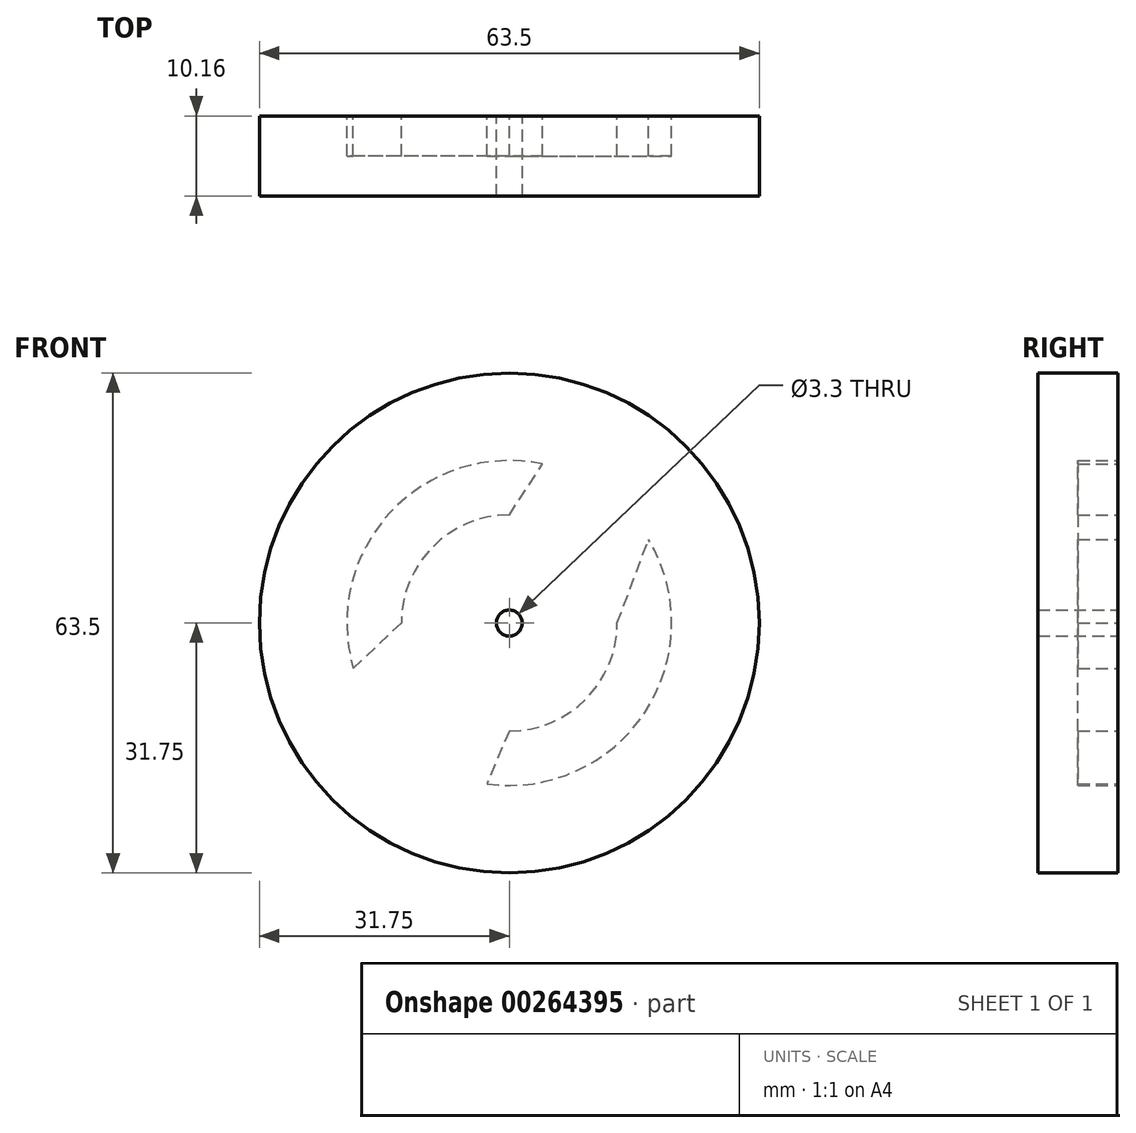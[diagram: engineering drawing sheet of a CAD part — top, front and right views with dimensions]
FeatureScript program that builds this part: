
annotation { "Feature Type Name" : "Feature", "Feature Type Description" : "" }
export const myFeature = defineFeature(function(context is Context, id is Id, definition is map)
    precondition{}
    {
        {
            var Q0;
            Q0=qCreatedBy(makeId("Front.planeOp"),FACE);
            var sketch = newSketch(context, id + "F0", { "sketchPlane" : qUnion([Q0])});
            skCircle(sketch, "E0", {"center": v(0, 0) * mm, "radius": 31.75 * mm});
            skCircle(sketch, "E1", {"center": v(0, 0) * mm, "radius": 1.65 * mm});
            skSolve(sketch);
        }
        {
            var Q0;
            Q0 = qSketchRegion(id + "F0", true);
            extrude(context, id + "F1", {"entities" : qUnion([Q0]), "depth" : 10.16 * mm});
        }
        {
            var Q0;
            Q0=qCreatedBy(makeId("Front.planeOp"),FACE);
            var sketch = newSketch(context, id + "F2", { "sketchPlane" : qUnion([Q0])});
            skArc(sketch, "E2", {"start": v(4.25, 20.2) * mm, "mid": v(-15.12, 14.04) * mm, "end": v(-19.82, -5.74) * mm});
            skArc(sketch, "E3", {"start": v(0, 13.71) * mm, "mid": v(-9.7, 9.7) * mm, "end": v(-13.71, 0) * mm});
            skLineSegment(sketch, "E4", {"start": v(0, 13.71) * mm, "end": v(4.25, 20.2) * mm});
            skLineSegment(sketch, "E5", {"start": v(-13.71, 0) * mm, "end": v(-19.82, -5.74) * mm});
            skLineSegment(sketch, "E6", {"start": v(0, -13.71) * mm, "end": v(-2.82, -20.44) * mm});
            skLineSegment(sketch, "E7", {"start": v(13.71, 0) * mm, "end": v(17.7, 10.6) * mm});
            skArc(sketch, "E8.trimOffspring", {"start": v(0, -13.71) * mm, "mid": v(9.7, -9.7) * mm, "end": v(13.71, 0) * mm});
            skArc(sketch, "E9.trimOffspring", {"start": v(-2.82, -20.44) * mm, "mid": v(17.21, -11.38) * mm, "end": v(17.7, 10.6) * mm});
            skSolve(sketch);
        }
        {
            var Q0;
            Q0 = qSketchRegion(id + "F2", true);
            extrude(context, id + "F3", {"entities" : qUnion([Q0]), "operationType" : NewBodyOperationType.REMOVE, "depth" : 5.08 * mm});
        }
    });
